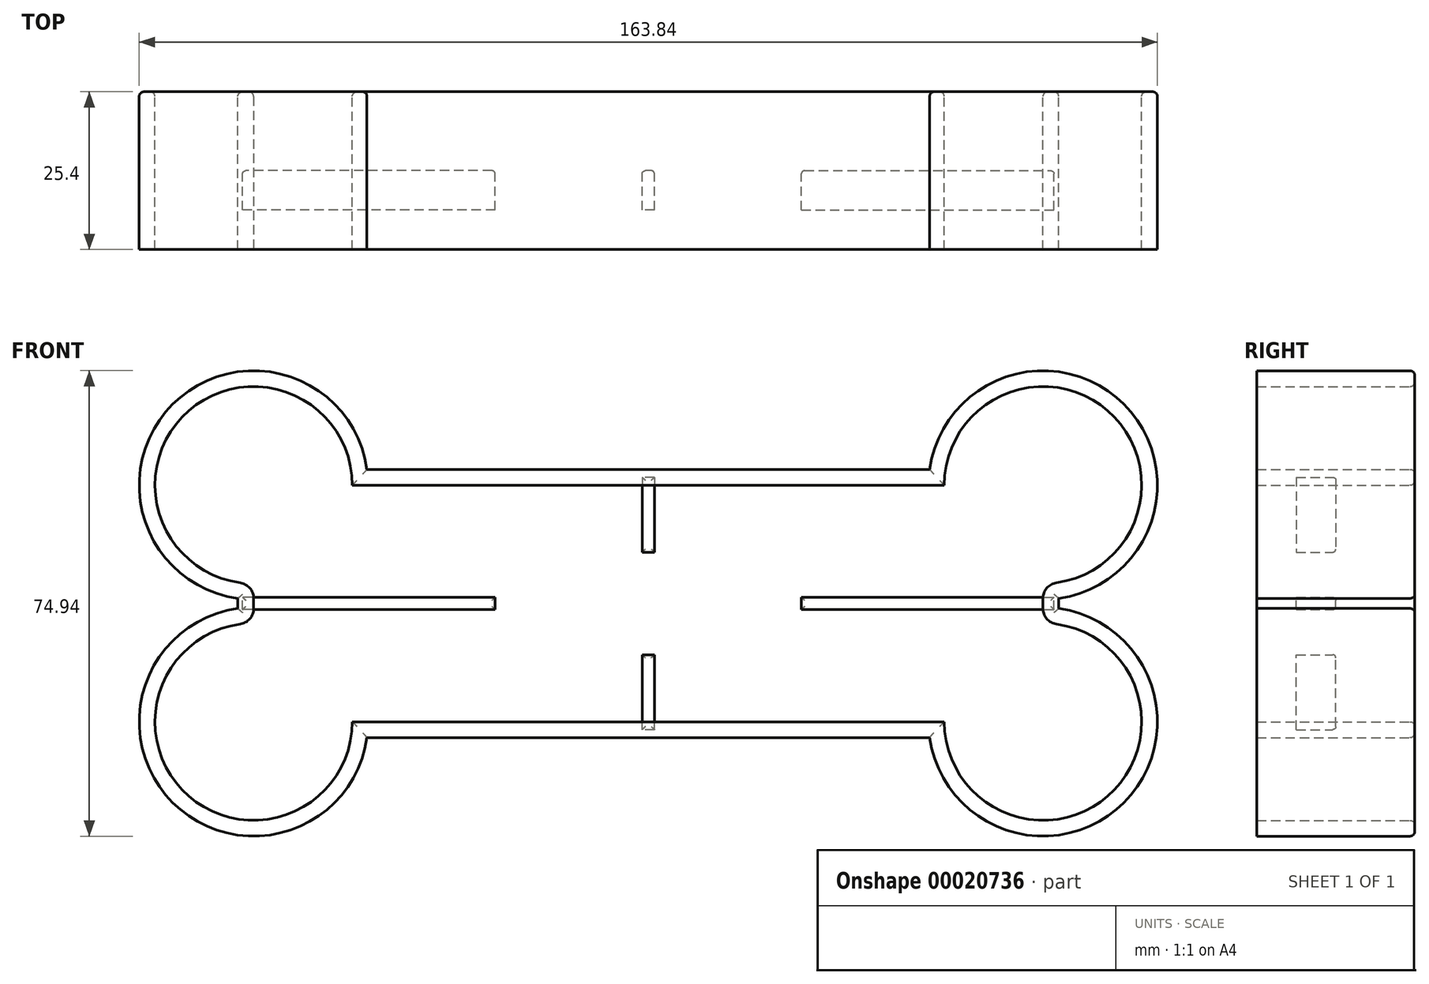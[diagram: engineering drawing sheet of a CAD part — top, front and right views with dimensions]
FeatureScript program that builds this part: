
annotation { "Feature Type Name" : "Feature", "Feature Type Description" : "" }
export const myFeature = defineFeature(function(context is Context, id is Id, definition is map)
    precondition{}
    {
        {
            var Q0;
            Q0=qCreatedBy(makeId("Front.planeOp"),FACE);
            var sketch = newSketch(context, id + "F0", { "sketchPlane" : qUnion([Q0])});
            skLineSegment(sketch, "E0.rect.bottom", {"start": v(63.5, 19.05) * mm, "end": v(-63.5, 19.05) * mm});
            skLineSegment(sketch, "E0.rect.top", {"start": v(63.5, -19.05) * mm, "end": v(-63.5, -19.05) * mm});
            skLineSegment(sketch, "E0.rect.left", {"start": v(63.5, 19.05) * mm, "end": v(63.5, -19.05) * mm});
            skLineSegment(sketch, "E0.rect.right", {"start": v(-63.5, 19.05) * mm, "end": v(-63.5, -19.05) * mm});
            skPoint(sketch, "E0.rect.middle", {"position": v(0, 0) * mm});
            skCircle(sketch, "E1", {"center": v(-63.5, 19.05) * mm, "radius": 15.88 * mm});
            skCircle(sketch, "E2", {"center": v(-63.5, -19.05) * mm, "radius": 15.88 * mm});
            skCircle(sketch, "E3", {"center": v(63.5, 19.05) * mm, "radius": 15.88 * mm});
            skCircle(sketch, "E4", {"center": v(63.5, -19.05) * mm, "radius": 15.88 * mm});
            skSolve(sketch);
        }
        {
            var Q0;
            Q0=qCreatedBy(makeId("Front.planeOp"),FACE);
            cPlane(context, id + "F1", {"entities" : qUnion([Q0]), "cplaneType" : CPlaneType.OFFSET, "offset" : 12.7 * mm, "width" : 152.4 * mm, "height" : 152.4 * mm});
        }
        {
            var Q0;
            Q0 = qSketchRegion(id + "F0", true);
            extrude(context, id + "F2", {"entities" : qUnion([Q0]), "depth" : 25.4 * mm});
        }
        {
            var Q0;
            Q0=makeQuery(id+"F2.opExtrude","SWEPT_EDGE",EDGE,{"disambiguationData":[OSD([sQuery(id+"F0.wireOp",EDGE,"E0.rect.right"),sQuery(id+"F0.wireOp",EDGE,"E2")])]});
            fillet(context, id + "F3", {"entities" : qUnion([Q0]), "radius" : 2.54 * mm, "tangentPropagation" : true, "allowEdgeOverflow" : false});
        }
        {
            var Q0;
            Q0=makeQuery(id+"F2.opExtrude","SWEPT_EDGE",EDGE,{"disambiguationData":[OSD([sQuery(id+"F0.wireOp",EDGE,"E0.rect.right"),sQuery(id+"F0.wireOp",EDGE,"E1")])]});
            var Q1;
            Q1=makeQuery(id+"F2.opExtrude","SWEPT_EDGE",EDGE,{"disambiguationData":[OSD([sQuery(id+"F0.wireOp",EDGE,"E0.rect.left"),sQuery(id+"F0.wireOp",EDGE,"E3")])]});
            var Q2;
            Q2=makeQuery(id+"F2.opExtrude","SWEPT_EDGE",EDGE,{"disambiguationData":[OSD([sQuery(id+"F0.wireOp",EDGE,"E0.rect.left"),sQuery(id+"F0.wireOp",EDGE,"E4")])]});
            fillet(context, id + "F4", {"entities" : qUnion([Q0, Q1, Q2]), "radius" : 2.54 * mm, "tangentPropagation" : true, "allowEdgeOverflow" : false});
        }
        {
            var Q0;
            Q0=makeQuery(id+"F2.opExtrude","CAP_FACE",FACE,{"disambiguationData":[OSD([sQuery(id+"F0.wireOp",EDGE,"E0.rect.bottom"),sQuery(id+"F0.wireOp",EDGE,"E0.rect.top"),sQuery(id+"F0.wireOp",EDGE,"E0.rect.left"),sQuery(id+"F0.wireOp",EDGE,"E0.rect.right"),sQuery(id+"F0.wireOp",EDGE,"E1"),sQuery(id+"F0.wireOp",EDGE,"E2"),sQuery(id+"F0.wireOp",EDGE,"E3"),sQuery(id+"F0.wireOp",EDGE,"E4")])],"isStart":true});
            var Q1;
            Q1=makeQuery(id+"F2.opExtrude","CAP_FACE",FACE,{"disambiguationData":[OSD([sQuery(id+"F0.wireOp",EDGE,"E0.rect.bottom"),sQuery(id+"F0.wireOp",EDGE,"E0.rect.top"),sQuery(id+"F0.wireOp",EDGE,"E0.rect.left"),sQuery(id+"F0.wireOp",EDGE,"E0.rect.right"),sQuery(id+"F0.wireOp",EDGE,"E1"),sQuery(id+"F0.wireOp",EDGE,"E2"),sQuery(id+"F0.wireOp",EDGE,"E3"),sQuery(id+"F0.wireOp",EDGE,"E4")])],"isStart":false});
            shell(context, id + "F5", {"entities" : qUnion([Q0, Q1]), "thickness" : 2.54 * mm, "oppositeDirection" : true});
        }
        {
            var Q0;
            Q0=qCreatedBy(id+"F1.planeOp",FACE);
            var sketch = newSketch(context, id + "F6", { "sketchPlane" : qUnion([Q0])});
            skLineSegment(sketch, "E5.rect.bottom", {"start": v(1, 20.32) * mm, "end": v(-1, 20.32) * mm});
            skLineSegment(sketch, "E5.rect.top", {"start": v(1, 8.26) * mm, "end": v(-1, 8.26) * mm});
            skLineSegment(sketch, "E5.rect.left", {"start": v(1, 20.32) * mm, "end": v(1, 8.26) * mm});
            skLineSegment(sketch, "E5.rect.right", {"start": v(-1, 20.32) * mm, "end": v(-1, 8.26) * mm});
            skPoint(sketch, "E5.rect.middle", {"position": v(0, 14.29) * mm});
            skSolve(sketch);
        }
        {
            var Q0;
            Q0 = qSketchRegion(id + "F6", true);
            extrude(context, id + "F7", {"entities" : qUnion([Q0]), "depth" : 6.35 * mm});
        }
        {
            var Q0;
            Q0=makeQuery(id+"F7.opExtrude","SWEPT_BODY",BODY,{"disambiguationData":[OSD([sQuery(id+"F6.wireOp",EDGE,"E5.rect.bottom"),sQuery(id+"F6.wireOp",EDGE,"E5.rect.top"),sQuery(id+"F6.wireOp",EDGE,"E5.rect.left"),sQuery(id+"F6.wireOp",EDGE,"E5.rect.right")])]});
            var Q1;
            Q1=qCreatedBy(makeId("Top.planeOp"),FACE);
            mirror(context, id + "F8", {"entities" : qUnion([Q0]), "mirrorPlane" : qUnion([Q1])});
        }
        {
            var Q0;
            Q0=qCreatedBy(id+"F1.planeOp",FACE);
            var sketch = newSketch(context, id + "F9", { "sketchPlane" : qUnion([Q0])});
            skLineSegment(sketch, "E6.rect.bottom", {"start": v(-24.64, -1) * mm, "end": v(-65.28, -1) * mm});
            skLineSegment(sketch, "E6.rect.top", {"start": v(-24.64, 1) * mm, "end": v(-65.28, 1) * mm});
            skLineSegment(sketch, "E6.rect.left", {"start": v(-24.64, -1) * mm, "end": v(-24.64, 1) * mm});
            skLineSegment(sketch, "E6.rect.right", {"start": v(-65.28, -1) * mm, "end": v(-65.28, 1) * mm});
            skPoint(sketch, "E6.rect.middle", {"position": v(-44.96, 0) * mm});
            skSolve(sketch);
        }
        {
            var Q0;
            Q0 = qSketchRegion(id + "F9", true);
            extrude(context, id + "F10", {"entities" : qUnion([Q0]), "depth" : 6.35 * mm});
        }
        {
            var Q0;
            Q0=makeQuery(id+"F10.opExtrude","SWEPT_BODY",BODY,{"disambiguationData":[OSD([sQuery(id+"F9.wireOp",EDGE,"E6.rect.bottom"),sQuery(id+"F9.wireOp",EDGE,"E6.rect.top"),sQuery(id+"F9.wireOp",EDGE,"E6.rect.left"),sQuery(id+"F9.wireOp",EDGE,"E6.rect.right")])]});
            var Q1;
            Q1=qCreatedBy(makeId("Right.planeOp"),FACE);
            mirror(context, id + "F11", {"entities" : qUnion([Q0]), "mirrorPlane" : qUnion([Q1])});
        }
        {
            var Q0;
            Q0=makeQuery(id+"F10.opExtrude","CAP_FACE",FACE,{"disambiguationData":[OSD([sQuery(id+"F9.wireOp",EDGE,"E6.rect.bottom"),sQuery(id+"F9.wireOp",EDGE,"E6.rect.top"),sQuery(id+"F9.wireOp",EDGE,"E6.rect.left"),sQuery(id+"F9.wireOp",EDGE,"E6.rect.right")])],"isStart":true});
            fillet(context, id + "F12", {"entities" : qUnion([Q0]), "radius" : 0.5 * mm, "tangentPropagation" : true, "allowEdgeOverflow" : false});
        }
        {
            var Q0;
            Q0=makeQuery(id+"F11.opPattern","COPY",FACE,{"derivedFrom":makeQuery(id+"F10.opExtrude","CAP_FACE",FACE,{"disambiguationData":[OSD([sQuery(id+"F9.wireOp",EDGE,"E6.rect.bottom"),sQuery(id+"F9.wireOp",EDGE,"E6.rect.top"),sQuery(id+"F9.wireOp",EDGE,"E6.rect.left"),sQuery(id+"F9.wireOp",EDGE,"E6.rect.right")])],"isStart":true}),"instanceName":"1"});
            fillet(context, id + "F13", {"entities" : qUnion([Q0]), "radius" : 0.5 * mm, "tangentPropagation" : true, "allowEdgeOverflow" : false});
        }
        {
            var Q0;
            Q0=makeQuery(id+"F8.opPattern","COPY",FACE,{"derivedFrom":makeQuery(id+"F7.opExtrude","CAP_FACE",FACE,{"disambiguationData":[OSD([sQuery(id+"F6.wireOp",EDGE,"E5.rect.bottom"),sQuery(id+"F6.wireOp",EDGE,"E5.rect.top"),sQuery(id+"F6.wireOp",EDGE,"E5.rect.left"),sQuery(id+"F6.wireOp",EDGE,"E5.rect.right")])],"isStart":true}),"instanceName":"1"});
            var Q1;
            Q1=makeQuery(id+"F7.opExtrude","CAP_FACE",FACE,{"disambiguationData":[OSD([sQuery(id+"F6.wireOp",EDGE,"E5.rect.bottom"),sQuery(id+"F6.wireOp",EDGE,"E5.rect.top"),sQuery(id+"F6.wireOp",EDGE,"E5.rect.left"),sQuery(id+"F6.wireOp",EDGE,"E5.rect.right")])],"isStart":true});
            fillet(context, id + "F14", {"entities" : qUnion([Q0, Q1]), "radius" : 0.5 * mm, "tangentPropagation" : true, "allowEdgeOverflow" : false});
        }
        {
            var Q0;
            Q0=makeQuery(id+"F2.opExtrude","CAP_FACE",FACE,{"disambiguationData":[OSD([sQuery(id+"F0.wireOp",EDGE,"E0.rect.bottom"),sQuery(id+"F0.wireOp",EDGE,"E0.rect.top"),sQuery(id+"F0.wireOp",EDGE,"E0.rect.left"),sQuery(id+"F0.wireOp",EDGE,"E0.rect.right"),sQuery(id+"F0.wireOp",EDGE,"E1"),sQuery(id+"F0.wireOp",EDGE,"E2"),sQuery(id+"F0.wireOp",EDGE,"E3"),sQuery(id+"F0.wireOp",EDGE,"E4")])],"isStart":true});
            fillet(context, id + "F15", {"entities" : qUnion([Q0]), "radius" : 0.76 * mm, "tangentPropagation" : true, "allowEdgeOverflow" : false});
        }
    });
